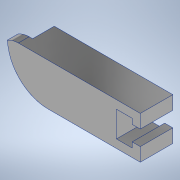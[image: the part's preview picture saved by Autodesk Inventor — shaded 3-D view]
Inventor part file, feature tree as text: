
AUTODESK INVENTOR PART (.ipt)
format: ipt  version: 2022 (Build 260153000, 153)  size: 163,840 bytes
history: native  units: mm
features: extrude x3, sketch x3, fillet x1
ambient origin geometry x8: Origin, YZ Plane, XZ Plane, XY Plane, X Axis, Y Axis, Z Axis, Center Point
bodies: Body1 (feature_tree)
feature tree (7):
  extrude  "Extrusion2"  Depth=5.8mm
  extrude  "Extrusion7"  Depth=12.0mm TaperAngle=0.0deg
  extrude  "Extrusion10"  Depth=15.6mm
  fillet  "Fillet2"  [1 undecoded]
  sketch  "Sketch5"  dims[d41=5.8mm d48=44.0mm]
  sketch  "Sketch11"  dims[d50=3.0mm d56=12.0mm d57=0.0mm]
  sketch  "Sketch14"  dims[d63=45.0mm d67=15.6mm d71=0.0mm d72=36.2mm d87=5.6mm d88=9.5mm d95=17.453293mm d96=5.0mm d97=10.0mm d98=8.0mm d99=0.0mm d107=5.5mm d108=0.0mm d109=0.0mm d110=15.0mm]
note: 1 required parameter value undecoded (feature->parameter linkage not recoverable at this tier; creation-order binding heuristic only, values carry confidence <= 0.55)
